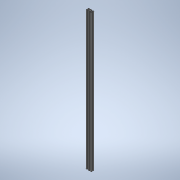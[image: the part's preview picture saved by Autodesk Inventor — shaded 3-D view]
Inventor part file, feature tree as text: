
AUTODESK INVENTOR PART (.ipt)
format: ipt  version: 2020 (Build 240168000, 168)  size: 419,328 bytes
history: native  units: mm
features: other x1, extrude x1, sketch x1
ambient origin geometry x8: Origin, YZ Plane, XZ Plane, XY Plane, X Axis, Y Axis, Z Axis, Center Point
bodies: Body1 (feature_tree)
feature tree (3):
  other  "Твердое тело1"
  extrude  "Выдавливание1"  Depth=0.25mm
  sketch  "Эскиз5"
